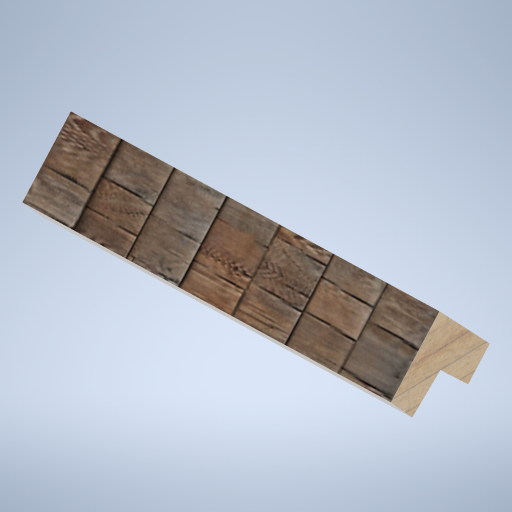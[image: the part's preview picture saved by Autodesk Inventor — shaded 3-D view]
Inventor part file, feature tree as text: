
AUTODESK INVENTOR PART (.ipt)
format: ipt  version: 2024.2 (Build 282272000, 272)  size: 516,096 bytes
history: native  units: mm
features: sketch x14, extrude x9, plane x6, projected_geometry x3, loft x1
ambient origin geometry x8: Origin, YZ Plane, XZ Plane, XY Plane, X Axis, Y Axis, Z Axis, Center Point
bodies: Solid1 (feature_tree)
feature tree (33):
  sketch  "Sketch1"  dims[d5=0.0mm d6=-7900.0mm d7=800.0mm]
  plane  "Work Plane2"
  loft  "Loft1"
  plane  "Work Plane3"
  extrude  "Extrusion1"  Depth=9000.0mm
  plane  "Work Plane4"
  sketch  "Sketch5"  dims[d12=800.0mm d13=0.0mm d14=90.0deg]
  plane  "Work Plane5"
  extrude  "Extrusion2"  Depth=9000.0mm
  plane  "Work Plane6"
  sketch  "Sketch7"  dims[d18=0.0mm d19=0.0mm d20=0.0mm]
  sketch  "Sketch8"  dims[d21=6.981317mm d22=0.0mm d23=0.0mm]
  extrude  "Extrusion3"  TaperAngle=0.0deg  [1 undecoded]
  sketch  "Sketch10"  dims[d31=120.0mm d32=120.0mm]
  extrude  "Extrusion5"  Depth=2500.0mm
  sketch  "Sketch16"  dims[d33=100.0mm d34=100.0mm]
  extrude  "Extrusion6"  TaperAngle=0.0deg  [1 undecoded]
  extrude  "Extrusion7"  TaperAngle=0.0deg  [1 undecoded]
  extrude  "Extrusion8"  Depth=1.0mm TaperAngle=0.0deg
  extrude  "Extrusion9"  Depth=120.0mm
  extrude  "Extrusion10"  Depth=100.0mm
  plane  "Work Plane1"
  sketch  "Sketch2"  dims[d8=9000.0mm d9=9000.0mm]
  sketch  "Sketch3"  dims[d10=9000.0mm d11=9000.0mm]
  sketch  "Sketch6"  dims[d15=0.0mm d16=90.0deg d17=2500.0mm]
  projected_geometry  "Projected Loop1"
  projected_geometry  "Projected Loop2"
  sketch  "Sketch9"  dims[d24=90.0deg d29=1.0mm d30=0.0mm]
  sketch  "Sketch17"  dims[d39=1100.0mm d40=0.0mm]
  sketch  "Sketch18"  dims[d41=2000.0mm d42=0.0mm]
  projected_geometry  "Projected Loop3"
  sketch  "Sketch19"  dims[d43=5000.0mm d44=0.0mm]
  sketch  "Sketch20"  dims[d45=5000.0mm d46=0.0mm d47=100.0mm d48=0.0mm d49=1100.0mm d50=0.0mm d35=500.0mm d36=0.872665mm d37=500.0mm d38=0.872665mm d51=500.0mm d52=0.872665mm]
note: 3 required parameter values undecoded (feature->parameter linkage not recoverable at this tier; creation-order binding heuristic only, values carry confidence <= 0.55)
